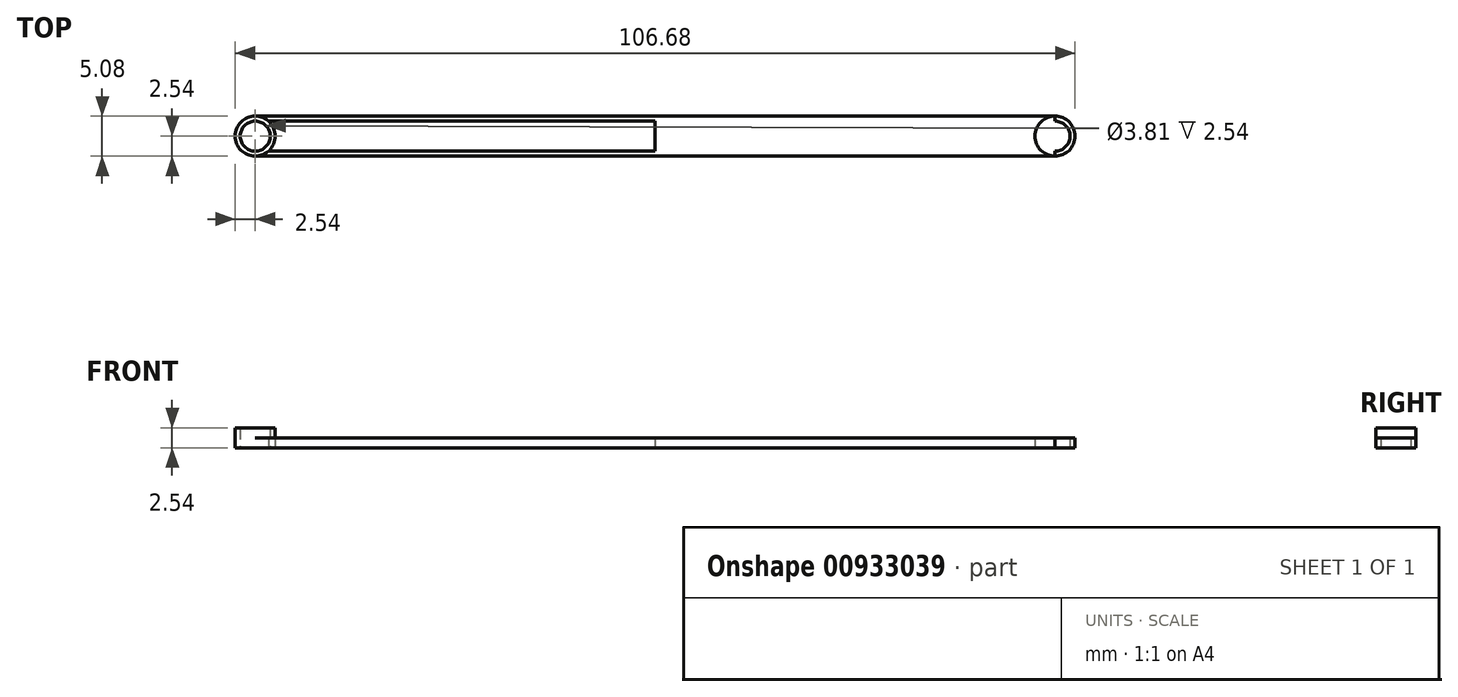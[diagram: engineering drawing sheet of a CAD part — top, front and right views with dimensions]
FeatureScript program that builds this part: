
annotation { "Feature Type Name" : "Feature", "Feature Type Description" : "" }
export const myFeature = defineFeature(function(context is Context, id is Id, definition is map)
    precondition{}
    {
        {
            var Q0;
            Q0=qCreatedBy(makeId("Top.planeOp"),FACE);
            var sketch = newSketch(context, id + "F0", { "sketchPlane" : qUnion([Q0])});
            skLineSegment(sketch, "E0.bottom", {"start": v(-50.8, 0) * mm, "end": v(0, 0) * mm});
            skLineSegment(sketch, "E0.top", {"start": v(-50.8, -5.08) * mm, "end": v(0, -5.08) * mm});
            skLineSegment(sketch, "E0.left", {"start": v(-50.8, 0) * mm, "end": v(-50.8, -5.08) * mm});
            skLineSegment(sketch, "E0.right", {"start": v(0, 0) * mm, "end": v(0, -5.08) * mm});
            skCircle(sketch, "E1", {"center": v(-50.8, -2.54) * mm, "radius": 1.9 * mm});
            skLineSegment(sketch, "E2", {"start": v(-50.8, -0.63) * mm, "end": v(0, -0.63) * mm});
            skLineSegment(sketch, "E3", {"start": v(-50.8, -4.44) * mm, "end": v(0, -4.44) * mm});
            skCircle(sketch, "E4", {"center": v(-50.8, -2.54) * mm, "radius": 2.54 * mm});
            skLineSegment(sketch, "E5.MirrorCS", {"start": v(50.8, 0) * mm, "end": v(50.8, -5.08) * mm});
            skCircle(sketch, "E6.MirrorC", {"center": v(50.8, -2.54) * mm, "radius": 1.9 * mm});
            skCircle(sketch, "E7.MirrorC", {"center": v(50.8, -2.54) * mm, "radius": 2.54 * mm});
            skLineSegment(sketch, "E8.MirrorCS", {"start": v(50.8, 0) * mm, "end": v(0, 0) * mm});
            skLineSegment(sketch, "E9.MirrorCS", {"start": v(50.8, -0.63) * mm, "end": v(0, -0.63) * mm});
            skLineSegment(sketch, "E10.MirrorCS", {"start": v(50.8, -5.08) * mm, "end": v(0, -5.08) * mm});
            skLineSegment(sketch, "E11.MirrorCS", {"start": v(50.8, -4.44) * mm, "end": v(0, -4.44) * mm});
            skSolve(sketch);
        }
        {
            var Q0;
            {var subQ0=sQuery(id+"F0.wireOp",EDGE,"E2");var subQ6=sQuery(id+"F0.wireOp",EDGE,"E4");var subQ7=makeQuery(id+"F0.imprint","INTERSECT",VERTEX,{"derivedFrom":[subQ0,subQ6]});Q0=makeQuery(id+"F0.imprint","IMPRINT",FACE,{"disambiguationData":[TD([[makeQuery(id+"F0.imprint","IMPRINT",EDGE,{"disambiguationData":[TD([[subQ7,1.0]])],"derivedFrom":subQ6}),1.0]])]});}
            var Q1;
            {var subQ0=sQuery(id+"F0.wireOp",EDGE,"E4");var subQ3=sQuery(id+"F0.wireOp",EDGE,"E2");var subQ5=makeQuery(id+"F0.imprint","INTERSECT",VERTEX,{"derivedFrom":[subQ3,subQ0]});Q1=makeQuery(id+"F0.imprint","IMPRINT",FACE,{"disambiguationData":[TD([[makeQuery(id+"F0.imprint","IMPRINT",EDGE,{"disambiguationData":[TD([[subQ5,1.0]])],"derivedFrom":subQ3}),1.0]])]});}
            var Q2;
            {var subQ0=sQuery(id+"F0.wireOp",EDGE,"E4");var subQ1=sQuery(id+"F0.wireOp",EDGE,"E0.left");var subQ2=makeQuery(id+"F0.imprint","INTERSECT",VERTEX,{"derivedFrom":[sQuery(id+"F0.wireOp",EDGE,"E0.bottom"),subQ1,subQ0]});Q2=makeQuery(id+"F0.imprint","IMPRINT",FACE,{"disambiguationData":[TD([[makeQuery(id+"F0.imprint","IMPRINT",EDGE,{"disambiguationData":[TD([[subQ2,-1.0]])],"derivedFrom":subQ1}),-1.0]])]});}
            var Q3;
            {var subQ0=sQuery(id+"F0.wireOp",EDGE,"E4");var subQ3=sQuery(id+"F0.wireOp",EDGE,"E3");var subQ5=makeQuery(id+"F0.imprint","INTERSECT",VERTEX,{"derivedFrom":[subQ3,subQ0]});Q3=makeQuery(id+"F0.imprint","IMPRINT",FACE,{"disambiguationData":[TD([[makeQuery(id+"F0.imprint","IMPRINT",EDGE,{"disambiguationData":[TD([[subQ5,1.0]])],"derivedFrom":subQ3}),-1.0]])]});}
            extrude(context, id + "F1", {"entities" : qUnion([Q0, Q1, Q2, Q3]), "depth" : 2.54 * mm, "offsetDistance" : 25.4 * mm});
        }
        {
            var Q0;
            {var subQ0=sQuery(id+"F0.wireOp",EDGE,"E0.bottom");Q0=makeQuery(id+"F0.imprint","IMPRINT",FACE,{"disambiguationData":[TD([[makeQuery(id+"F0.imprint","IMPRINT",EDGE,{"derivedFrom":subQ0}),-1.0]])]});}
            var Q1;
            {var subQ0=sQuery(id+"F0.wireOp",EDGE,"E0.top");Q1=makeQuery(id+"F0.imprint","IMPRINT",FACE,{"disambiguationData":[TD([[makeQuery(id+"F0.imprint","IMPRINT",EDGE,{"derivedFrom":subQ0}),1.0]])]});}
            var Q2;
            {var subQ0=sQuery(id+"F0.wireOp",EDGE,"E7.MirrorC");var subQ1=sQuery(id+"F0.wireOp",EDGE,"E5.MirrorCS");var subQ2=makeQuery(id+"F0.imprint","INTERSECT",VERTEX,{"derivedFrom":[subQ1,subQ0,sQuery(id+"F0.wireOp",EDGE,"E8.MirrorCS")]});Q2=makeQuery(id+"F0.imprint","IMPRINT",FACE,{"disambiguationData":[TD([[makeQuery(id+"F0.imprint","IMPRINT",EDGE,{"disambiguationData":[TD([[subQ2,-1.0]])],"derivedFrom":subQ1}),1.0]])]});}
            var Q3;
            {var subQ0=sQuery(id+"F0.wireOp",EDGE,"E8.MirrorCS");Q3=makeQuery(id+"F0.imprint","IMPRINT",FACE,{"disambiguationData":[TD([[makeQuery(id+"F0.imprint","IMPRINT",EDGE,{"derivedFrom":subQ0}),1.0]])]});}
            var Q4;
            {var subQ0=sQuery(id+"F0.wireOp",EDGE,"E7.MirrorC");var subQ3=sQuery(id+"F0.wireOp",EDGE,"E9.MirrorCS");var subQ5=makeQuery(id+"F0.imprint","INTERSECT",VERTEX,{"derivedFrom":[subQ0,subQ3]});Q4=makeQuery(id+"F0.imprint","IMPRINT",FACE,{"disambiguationData":[TD([[makeQuery(id+"F0.imprint","IMPRINT",EDGE,{"disambiguationData":[TD([[subQ5,-1.0]])],"derivedFrom":subQ0}),-1.0]])]});}
            var Q5;
            {var subQ0=sQuery(id+"F0.wireOp",EDGE,"E7.MirrorC");var subQ3=sQuery(id+"F0.wireOp",EDGE,"E11.MirrorCS");var subQ5=makeQuery(id+"F0.imprint","INTERSECT",VERTEX,{"derivedFrom":[subQ0,subQ3]});Q5=makeQuery(id+"F0.imprint","IMPRINT",FACE,{"disambiguationData":[TD([[makeQuery(id+"F0.imprint","IMPRINT",EDGE,{"disambiguationData":[TD([[subQ5,1.0]])],"derivedFrom":subQ0}),-1.0]])]});}
            var Q6;
            {var subQ0=sQuery(id+"F0.wireOp",EDGE,"E10.MirrorCS");Q6=makeQuery(id+"F0.imprint","IMPRINT",FACE,{"disambiguationData":[TD([[makeQuery(id+"F0.imprint","IMPRINT",EDGE,{"derivedFrom":subQ0}),-1.0]])]});}
            extrude(context, id + "F2", {"entities" : qUnion([Q0, Q1, Q2, Q3, Q4, Q5, Q6]), "operationType" : NewBodyOperationType.ADD, "depth" : 1.27 * mm, "offsetDistance" : 25.4 * mm});
        }
    });
